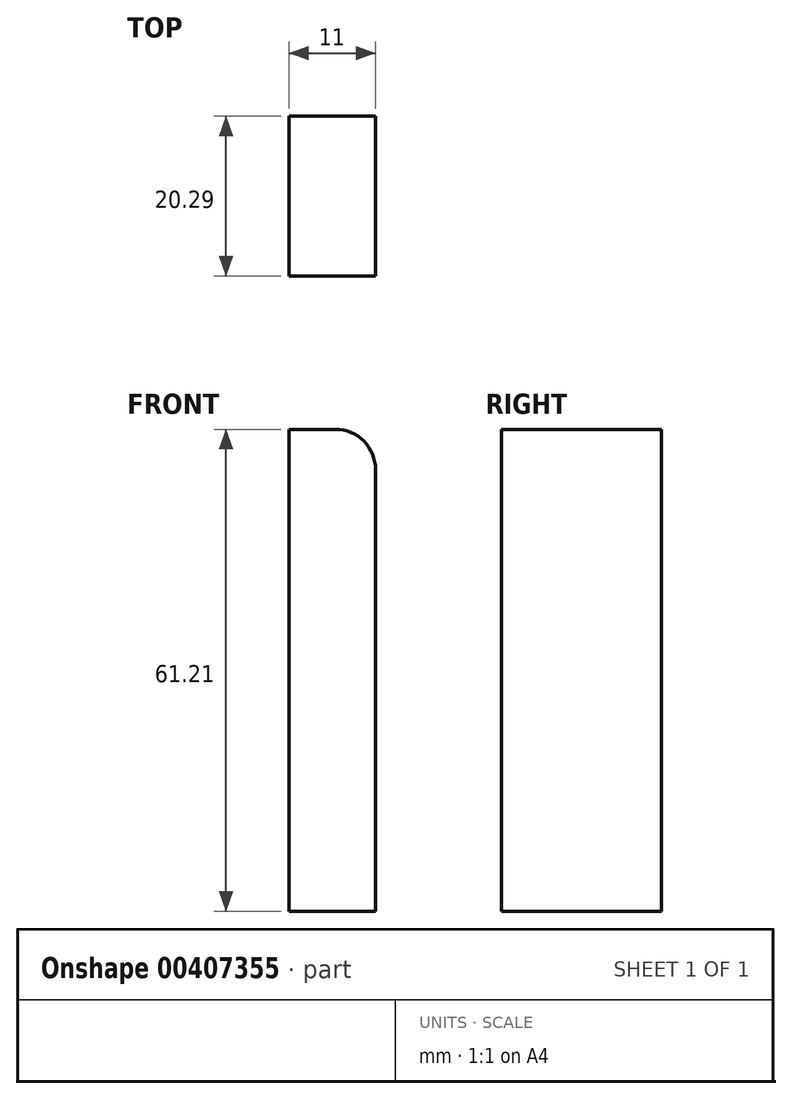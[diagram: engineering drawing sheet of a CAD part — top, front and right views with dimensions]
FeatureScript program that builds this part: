
annotation { "Feature Type Name" : "Feature", "Feature Type Description" : "" }
export const myFeature = defineFeature(function(context is Context, id is Id, definition is map)
    precondition{}
    {
        {
            var Q0;
            Q0=qCreatedBy(makeId("Top.planeOp"),FACE);
            var sketch = newSketch(context, id + "F0", { "sketchPlane" : qUnion([Q0])});
            skLineSegment(sketch, "E0.bottom", {"start": v(-46.26, 36.78) * mm, "end": v(39.82, 36.78) * mm});
            skLineSegment(sketch, "E0.top", {"start": v(-46.26, -32.42) * mm, "end": v(39.82, -32.42) * mm});
            skLineSegment(sketch, "E0.left", {"start": v(-46.26, 36.78) * mm, "end": v(-46.26, -32.42) * mm});
            skLineSegment(sketch, "E0.right", {"start": v(39.82, 36.78) * mm, "end": v(39.82, -32.42) * mm});
            skLineSegment(sketch, "E1.bottom", {"start": v(67.3, -25.79) * mm, "end": v(19.9, -25.79) * mm});
            skLineSegment(sketch, "E1.top", {"start": v(67.3, -12.7) * mm, "end": v(19.9, -12.7) * mm});
            skLineSegment(sketch, "E1.left", {"start": v(67.3, -25.79) * mm, "end": v(67.3, -12.7) * mm});
            skLineSegment(sketch, "E1.right", {"start": v(19.9, -25.79) * mm, "end": v(19.9, -12.7) * mm});
            skLineSegment(sketch, "E2.bottom", {"start": v(28.82, 62.19) * mm, "end": v(62.19, 62.19) * mm});
            skLineSegment(sketch, "E2.top", {"start": v(28.82, 16.5) * mm, "end": v(62.19, 16.5) * mm});
            skLineSegment(sketch, "E2.left", {"start": v(28.82, 62.19) * mm, "end": v(28.82, 16.5) * mm});
            skLineSegment(sketch, "E2.right", {"start": v(62.19, 62.19) * mm, "end": v(62.19, 16.5) * mm});
            skSolve(sketch);
        }
        {
            var Q0;
            {var subQ0=sQuery(id+"F0.wireOp",EDGE,"E0.right");var subQ1=sQuery(id+"F0.wireOp",EDGE,"E0.bottom");var subQ2=makeQuery(id+"F0.imprint","INTERSECT",VERTEX,{"derivedFrom":[subQ1,subQ0]});Q0=makeQuery(id+"F0.imprint","IMPRINT",FACE,{"disambiguationData":[TD([[makeQuery(id+"F0.imprint","IMPRINT",EDGE,{"disambiguationData":[TD([[subQ2,1.0]])],"derivedFrom":subQ1}),-1.0]])]});}
            extrude(context, id + "F1", {"entities" : qUnion([Q0]), "depth" : 61.2 * mm});
        }
        {
            var Q0;
            Q0=makeQuery(id+"F1.opExtrude","CAP_EDGE",EDGE,{"disambiguationData":[OSD([sQuery(id+"F0.wireOp",EDGE,"E0.right")])],"isStart":false});
            fillet(context, id + "F2", {"entities" : qUnion([Q0]), "radius" : 5.08 * mm, "tangentPropagation" : true, "allowEdgeOverflow" : false});
        }
    });
